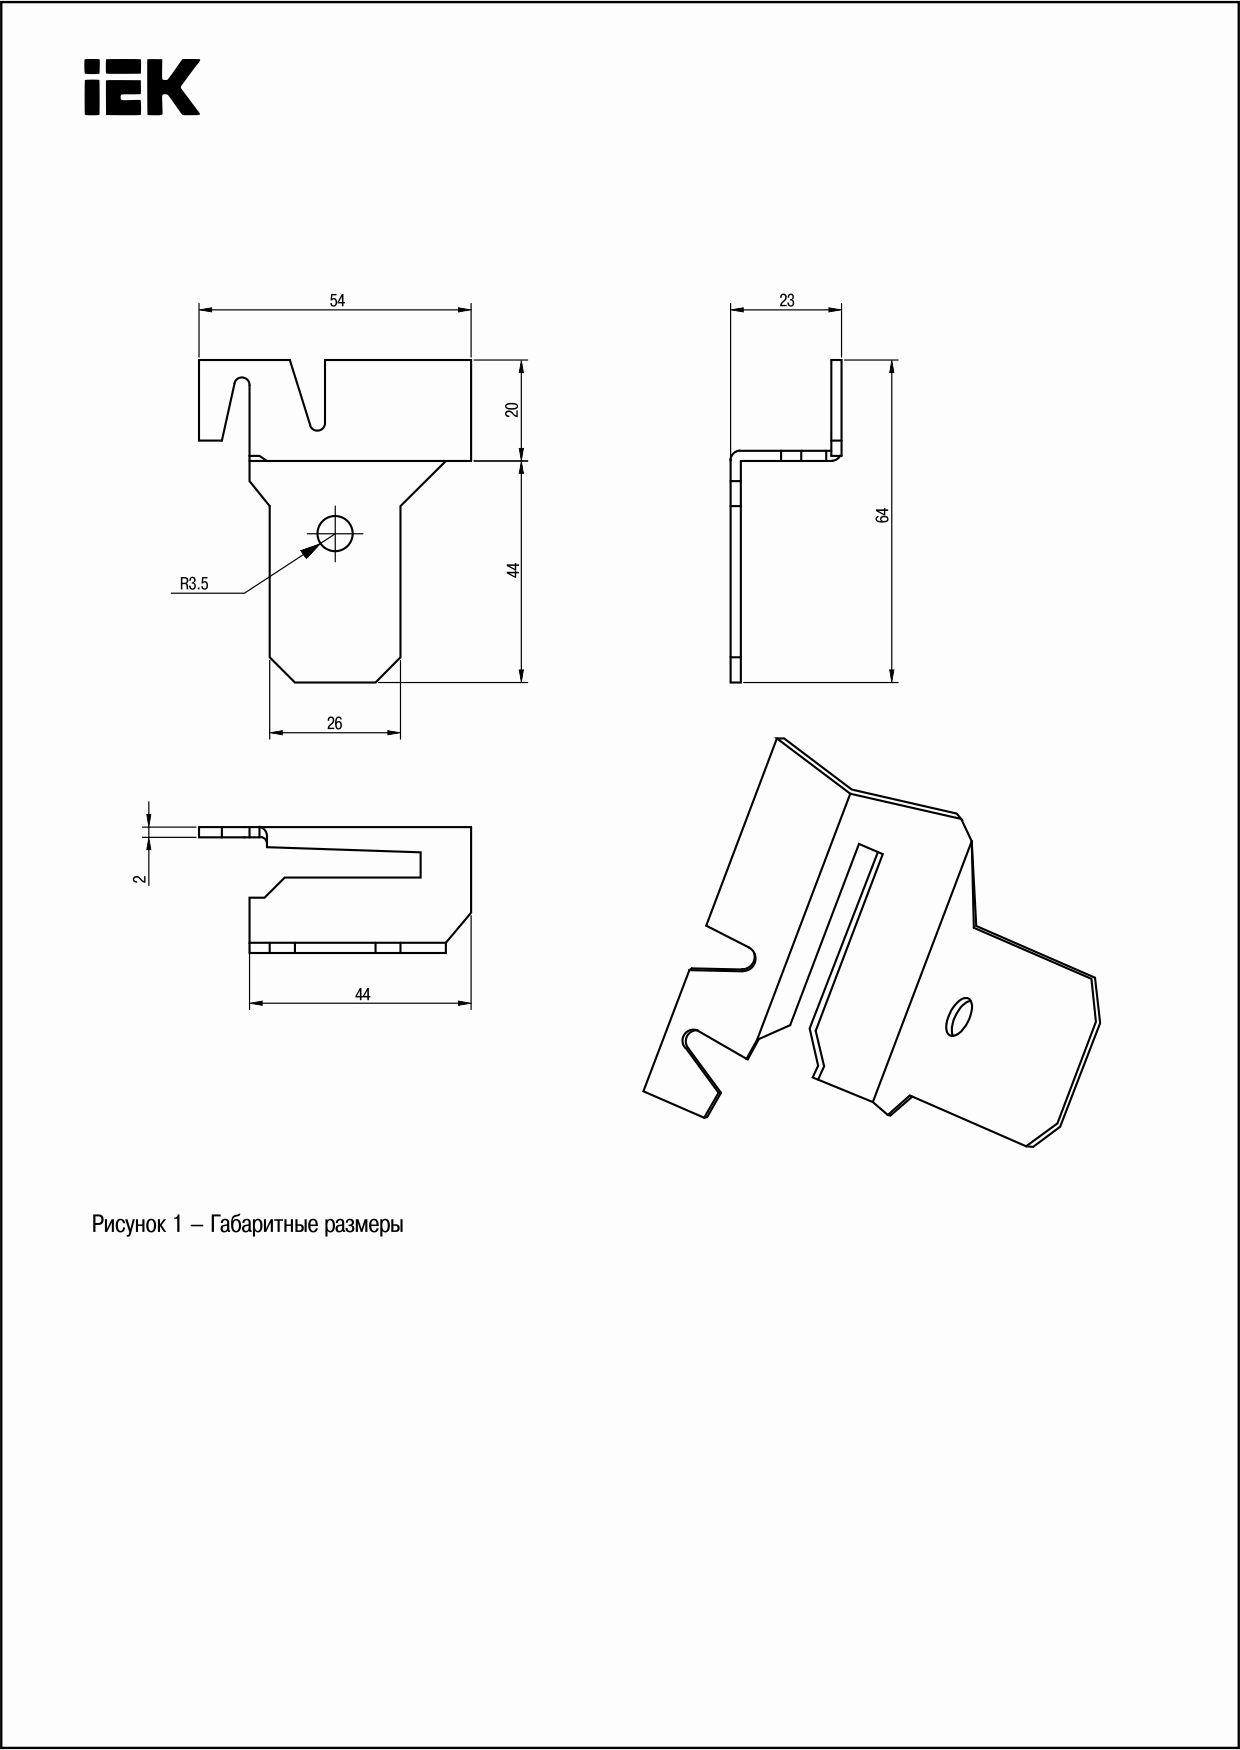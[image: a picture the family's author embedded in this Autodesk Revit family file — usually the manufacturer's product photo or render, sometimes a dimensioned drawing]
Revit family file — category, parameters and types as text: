
# Revit family: IEK_Держатель шин заземления
name_source: partatom
category: Обобщенные модели
units: mm (PartAtom-declared; Revit-internal decimal feet)

## family parameters
Может служить основой для арматурных стержней = Нет
Общий = Да
Основа = Грань
При загрузке вырезать с полостями = Нет
Размер круглого соединителя = Использовать диаметр
Тип детали = Нормальный
Точка расчета площади = Нет

## types (2) — shared parameters
ADSK_URL страницы изделия = https://www.iek.ru
ADSK_Версия Revit = 2019
ADSK_Версия семейства = 1.0
ADSK_Группирование = VIII. ЭЛЕМЕНТЫ ВНЕШНЕЙ МОЛНИЕЗАЩИТЫ
ADSK_Единица измерения = шт
ADSK_Завод-изготовитель = IEK
ADSK_Масса = 0.05
IEK_URL = https://www.iek.ru
IEK_Описание = Удобная форма изделия позволяет быстро производить монтаж шин.
zero-valued in all types: Отметка по умолчанию

## per-type parameters (varying)
| type | ADSK_Код изделия | ADSK_Материал | ADSK_Материал наименование | ADSK_Наименование | IEK_Цена за единицу | KSI_CMa_Строительные материалы |
| Стальной | ZGB10D-BH-11 | Сталь оцинкованная | Сталь оцинкованная | Держатель шин заземления оцинкованная сталь IEK | 120 | 24.10.35.000.08.3.05.06-0001 |
| Медный | ZGB10D-BH-50 | Медь | Медь | Держатель шин заземления медь IEK | 527.8 | СТ 10 12 20 10 |
